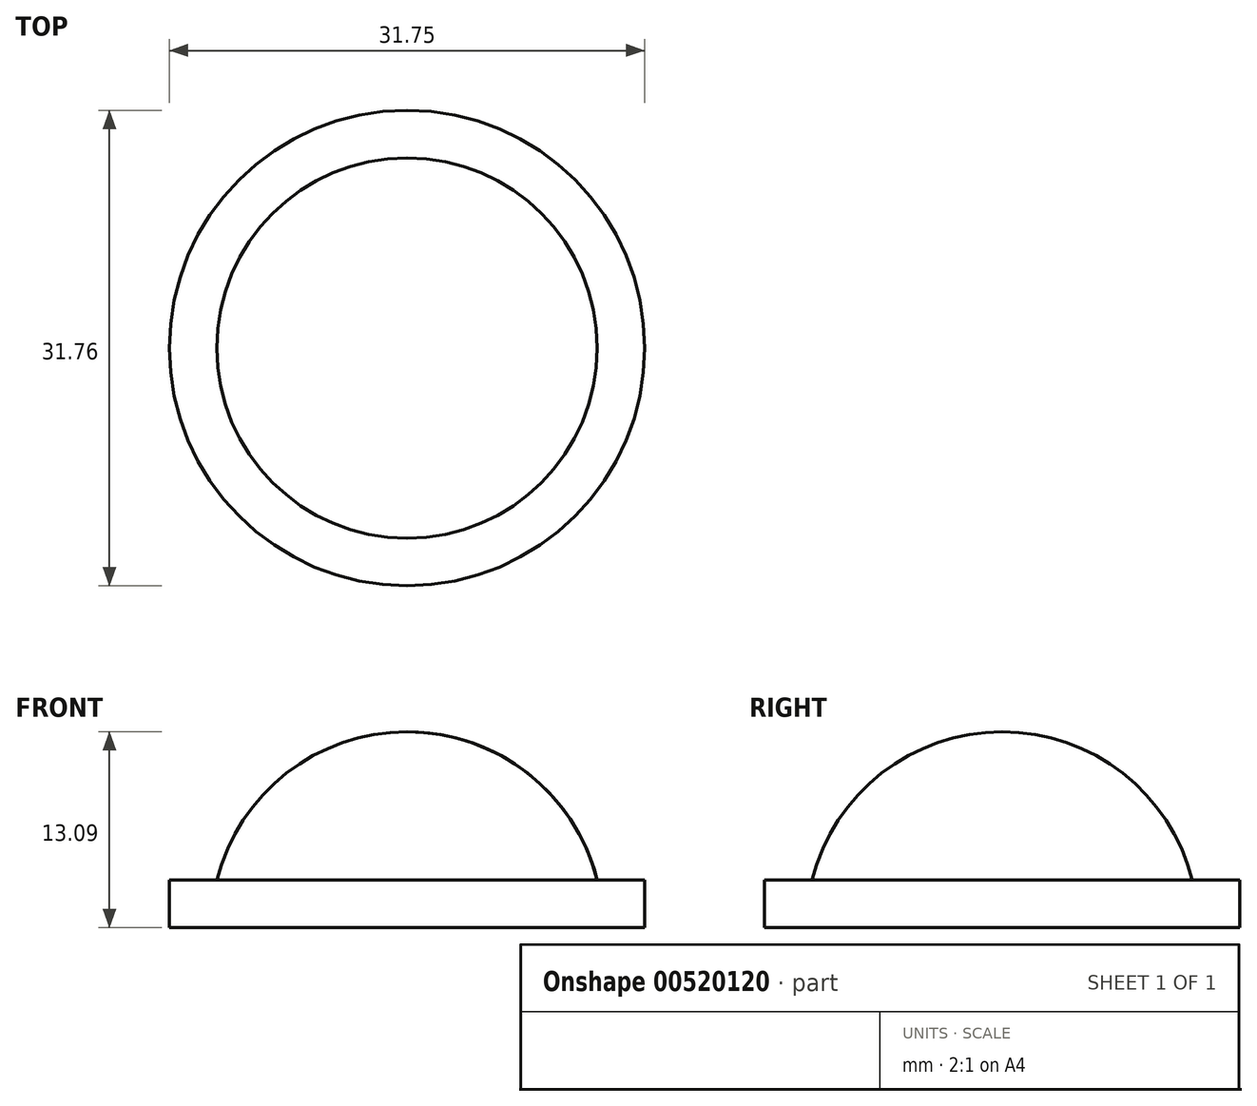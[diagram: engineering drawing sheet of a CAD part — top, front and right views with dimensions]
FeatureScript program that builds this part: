
annotation { "Feature Type Name" : "Feature", "Feature Type Description" : "" }
export const myFeature = defineFeature(function(context is Context, id is Id, definition is map)
    precondition{}
    {
        {
            var Q0;
            Q0=qCreatedBy(makeId("Front.planeOp"),FACE);
            var sketch = newSketch(context, id + "F0", { "sketchPlane" : qUnion([Q0])});
            skLineSegment(sketch, "E0", {"start": v(-15.88, 0) * mm, "end": v(-31.75, 0) * mm});
            skLineSegment(sketch, "E1", {"start": v(-31.75, 0) * mm, "end": v(-31.75, 3.17) * mm});
            skLineSegment(sketch, "E2", {"start": v(-31.75, 3.17) * mm, "end": v(-28.57, 3.17) * mm});
            skLineSegment(sketch, "E3", {"start": v(-15.88, 0) * mm, "end": v(-15.88, 13.1) * mm});
            skArc(sketch, "E4", {"start": v(-28.57, 3.17) * mm, "mid": v(-23.93, 10.32) * mm, "end": v(-15.88, 13.1) * mm});
            skPoint(sketch, "E5.orphan", {"position": v(0, 0) * mm});
            skSolve(sketch);
        }
        {
            var Q0;
            Q0=makeQuery(id+"F0.imprint","IMPRINT",FACE,{"disambiguationData":[TD([[makeQuery(id+"F0.imprint","IMPRINT",EDGE,{"derivedFrom":sQuery(id+"F0.wireOp",EDGE,"E0")}),-1.0]])]});
            var Q1;
            Q1=sQuery(id+"F0.wireOp",EDGE,"E3");
            revolve(context, id + "F1", {"entities" : qUnion([Q0]), "axis" : qUnion([Q1]), "revolveType" : RevolveType.FULL});
        }
    });
